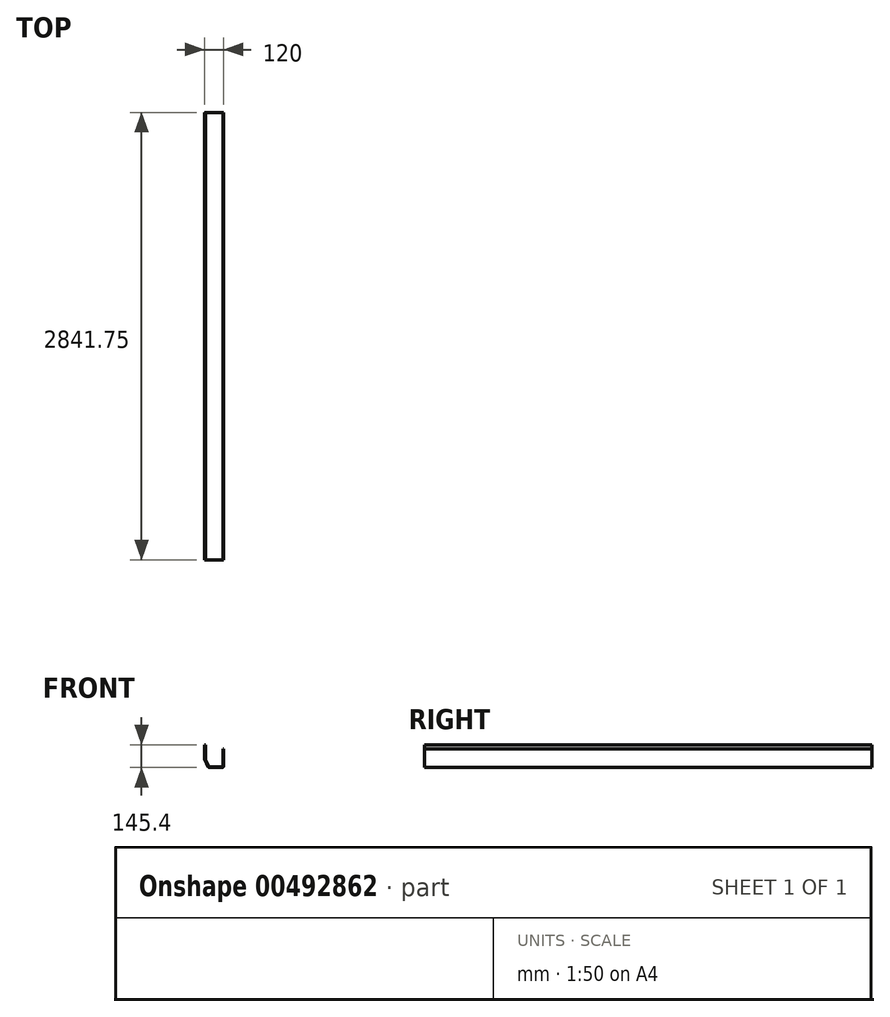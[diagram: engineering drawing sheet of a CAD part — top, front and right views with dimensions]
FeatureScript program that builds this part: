
annotation { "Feature Type Name" : "Feature", "Feature Type Description" : "" }
export const myFeature = defineFeature(function(context is Context, id is Id, definition is map)
    precondition{}
    {
        {
            var Q0;
            Q0=qCreatedBy(makeId("Front.planeOp"),FACE);
            var sketch = newSketch(context, id + "F0", { "sketchPlane" : qUnion([Q0])});
            skLineSegment(sketch, "E0", {"start": v(0, 0) * mm, "end": v(120, 0) * mm, "construction": true});
            skLineSegment(sketch, "E1", {"start": v(120, 10) * mm, "end": v(120, 119.4) * mm});
            skLineSegment(sketch, "E2", {"start": v(0, 0) * mm, "end": v(0, 145.4) * mm, "construction": true});
            skPoint(sketch, "E3", {"position": v(0, 51) * mm});
            skPoint(sketch, "E4", {"position": v(25, 0) * mm});
            skLineSegment(sketch, "E5", {"start": v(1.02, 48.92) * mm, "end": v(22.26, 5.6) * mm});
            skLineSegment(sketch, "E6", {"start": v(0, 145.4) * mm, "end": v(0, 53.32) * mm});
            skLineSegment(sketch, "E7", {"start": v(31.23, 0) * mm, "end": v(110, 0) * mm});
            skLineSegment(sketch, "E8.0", {"start": v(115.5, 14.5) * mm, "end": v(115.5, 119.4) * mm});
            skLineSegment(sketch, "E8.1", {"start": v(34.04, 4.5) * mm, "end": v(105.5, 4.5) * mm});
            skLineSegment(sketch, "E8.2", {"start": v(5.52, 49.96) * mm, "end": v(25.06, 10.1) * mm});
            skLineSegment(sketch, "E8.3", {"start": v(4.5, 145.4) * mm, "end": v(4.5, 54.36) * mm});
            skLineSegment(sketch, "E9", {"start": v(0, 145.4) * mm, "end": v(4.5, 145.4) * mm});
            skLineSegment(sketch, "E10", {"start": v(115.5, 119.4) * mm, "end": v(120, 119.4) * mm});
            skPoint(sketch, "E11.visualSharp", {"position": v(120, 0) * mm});
            skArc(sketch, "E11.filletArc", {"start": v(110, 0) * mm, "mid": v(117.07, 2.93) * mm, "end": v(120, 10) * mm});
            skPoint(sketch, "E12.visualSharp", {"position": v(115.5, 4.5) * mm});
            skArc(sketch, "E12.filletArc", {"start": v(105.5, 4.5) * mm, "mid": v(112.57, 7.43) * mm, "end": v(115.5, 14.5) * mm});
            skPoint(sketch, "E13.visualSharp", {"position": v(27.8, 4.5) * mm});
            skArc(sketch, "E13.filletArc", {"start": v(25.06, 10.1) * mm, "mid": v(28.75, 6.01) * mm, "end": v(34.04, 4.5) * mm});
            skArc(sketch, "E14.filletArc", {"start": v(22.26, 5.6) * mm, "mid": v(25.94, 1.51) * mm, "end": v(31.23, 0) * mm});
            skArc(sketch, "E15.filletArc", {"start": v(0, 53.32) * mm, "mid": v(0.26, 51.06) * mm, "end": v(1.02, 48.92) * mm});
            skPoint(sketch, "E16.visualSharp", {"position": v(4.5, 52.04) * mm});
            skArc(sketch, "E16.filletArc", {"start": v(4.5, 54.36) * mm, "mid": v(4.76, 52.1) * mm, "end": v(5.52, 49.96) * mm});
            skSolve(sketch);
        }
        {
            var Q0;
            Q0=makeQuery(id+"F0.imprint","IMPRINT",FACE,{"disambiguationData":[TD([[makeQuery(id+"F0.imprint","IMPRINT",EDGE,{"derivedFrom":sQuery(id+"F0.wireOp",EDGE,"E1")}),1.0]])]});
            extrude(context, id + "F1", {"entities" : qUnion([Q0]), "depth" : 2841.75 * mm});
        }
    });
